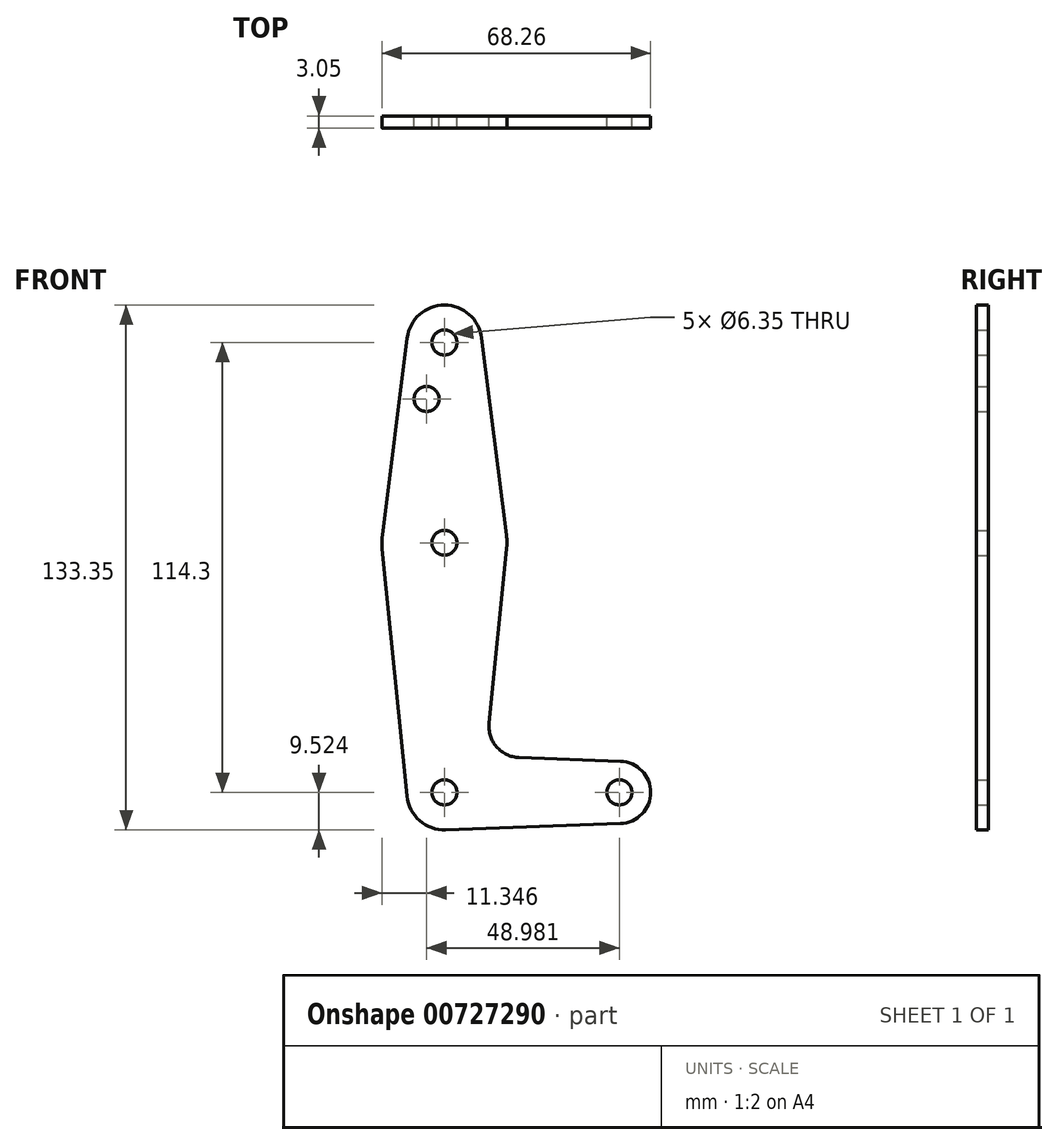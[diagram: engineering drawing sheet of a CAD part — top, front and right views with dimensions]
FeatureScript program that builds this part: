
annotation { "Feature Type Name" : "Feature", "Feature Type Description" : "" }
export const myFeature = defineFeature(function(context is Context, id is Id, definition is map)
    precondition{}
    {
        {
            var Q0;
            Q0=qCreatedBy(makeId("Front.planeOp"),FACE);
            var sketch = newSketch(context, id + "F0", { "sketchPlane" : qUnion([Q0])});
            skLineSegment(sketch, "E0", {"start": v(-45.14, 79.17) * mm, "end": v(-45.14, -35.13) * mm, "construction": true});
            skLineSegment(sketch, "E1", {"start": v(-45.14, -35.13) * mm, "end": v(-0.7, -35.13) * mm, "construction": true});
            skArc(sketch, "E2", {"start": v(-54.62, -36.08) * mm, "mid": v(-51.4, -42.3) * mm, "end": v(-44.8, -44.65) * mm});
            skArc(sketch, "E3", {"start": v(-35.7, 80.36) * mm, "mid": v(-45.14, 88.7) * mm, "end": v(-54.6, 80.36) * mm});
            skCircle(sketch, "E4", {"center": v(-0.7, -35.13) * mm, "radius": 7.94 * mm});
            skArc(sketch, "E5", {"start": v(-29.35, 26.72) * mm, "mid": v(-29.27, 28.5) * mm, "end": v(-29.4, 30.29) * mm});
            skLineSegment(sketch, "E6", {"start": v(-35.7, 80.36) * mm, "end": v(-29.4, 30.29) * mm});
            skLineSegment(sketch, "E7", {"start": v(-54.6, 80.36) * mm, "end": v(-60.9, 30.29) * mm});
            skLineSegment(sketch, "E8", {"start": v(-60.94, 26.72) * mm, "end": v(-54.62, -36.08) * mm});
            skLineSegment(sketch, "E9", {"start": v(-29.35, 26.72) * mm, "end": v(-33.8, -17.53) * mm});
            skLineSegment(sketch, "E10", {"start": v(-26.17, -26.27) * mm, "end": v(-0.41, -27.2) * mm});
            skLineSegment(sketch, "E11", {"start": v(-44.8, -44.65) * mm, "end": v(-0.41, -43.06) * mm});
            skLineSegment(sketch, "E12.trimOffspring", {"start": v(-35.57, -35.13) * mm, "end": v(-35.67, -36.08) * mm});
            skArc(sketch, "E13.trimOffspring", {"start": v(-35.67, -36.08) * mm, "mid": v(-35.63, -35.6) * mm, "end": v(-35.62, -35.13) * mm});
            skArc(sketch, "E14.trimOffspring", {"start": v(-60.9, 30.29) * mm, "mid": v(-61.02, 28.5) * mm, "end": v(-60.94, 26.72) * mm});
            skPoint(sketch, "E15.visualSharp", {"position": v(-34.65, -25.97) * mm});
            skArc(sketch, "E15.filletArc", {"start": v(-33.8, -17.53) * mm, "mid": v(-31.88, -23.55) * mm, "end": v(-26.17, -26.27) * mm});
            skCircle(sketch, "E16", {"center": v(-45.14, 28.3) * mm, "radius": 3.18 * mm});
            skCircle(sketch, "E17", {"center": v(-45.14, -35.13) * mm, "radius": 3.18 * mm});
            skCircle(sketch, "E18", {"center": v(-0.7, -35.13) * mm, "radius": 3.18 * mm});
            skCircle(sketch, "E19", {"center": v(-45.14, 79.17) * mm, "radius": 3.18 * mm});
            skCircle(sketch, "E20", {"center": v(-49.67, 64.83) * mm, "radius": 3.18 * mm});
            skSolve(sketch);
        }
        {
            var Q0;
            Q0 = qSketchRegion(id + "F0", true);
            extrude(context, id + "F1", {"entities" : qUnion([Q0]), "depth" : 3.05 * mm, "offsetDistance" : 25.4 * mm});
        }
    });
